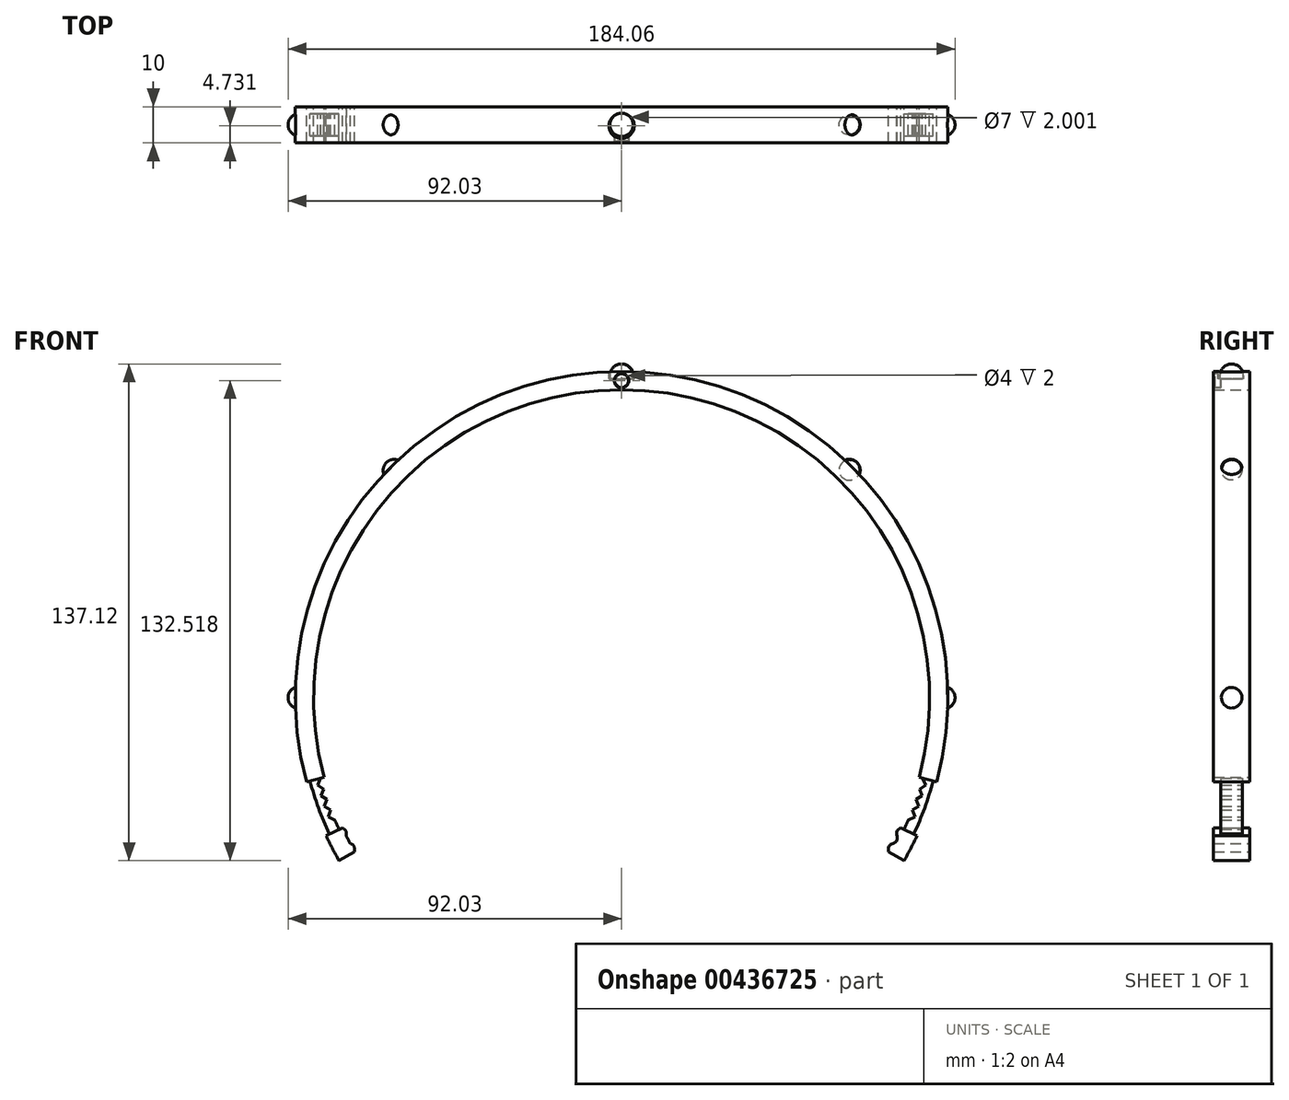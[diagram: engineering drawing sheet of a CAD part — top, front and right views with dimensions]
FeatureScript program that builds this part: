
annotation { "Feature Type Name" : "Feature", "Feature Type Description" : "" }
export const myFeature = defineFeature(function(context is Context, id is Id, definition is map)
    precondition{}
    {
        {
            var Q0;
            Q0=qCreatedBy(makeId("Front.planeOp"),FACE);
            var sketch = newSketch(context, id + "F0", { "sketchPlane" : qUnion([Q0])});
            skArc(sketch, "E0", {"start": v(82.1, -22) * mm, "mid": v(0, 85) * mm, "end": v(-82.1, -22) * mm});
            skArc(sketch, "E1", {"start": v(86.93, -23.3) * mm, "mid": v(0, 90) * mm, "end": v(-86.93, -23.3) * mm});
            skLineSegment(sketch, "E2", {"start": v(-86.93, -23.3) * mm, "end": v(-82.1, -22) * mm});
            skLineSegment(sketch, "E3", {"start": v(82.1, -22) * mm, "end": v(86.93, -23.3) * mm});
            skSolve(sketch);
        }
        {
            var Q0;
            Q0=makeQuery(id+"F0.imprint","IMPRINT",FACE,{"disambiguationData":[TD([[makeQuery(id+"F0.imprint","IMPRINT",EDGE,{"derivedFrom":sQuery(id+"F0.wireOp",EDGE,"E0")}),-1.0]])]});
            extrude(context, id + "F1", {"entities" : qUnion([Q0]), "depth" : 10 * mm});
        }
        {
            var Q0;
            Q0=qCreatedBy(makeId("Front.planeOp"),FACE);
            cPlane(context, id + "F2", {"entities" : qUnion([Q0]), "cplaneType" : CPlaneType.OFFSET, "offset" : 2 * mm, "width" : 150 * mm, "height" : 150 * mm});
        }
        {
            var Q0;
            Q0=qCreatedBy(id+"F2.planeOp",FACE);
            var sketch = newSketch(context, id + "F3", { "sketchPlane" : qUnion([Q0])});
            skLineSegment(sketch, "E4", {"start": v(83.07, -22.26) * mm, "end": v(85.97, -23.03) * mm});
            skArc(sketch, "E5", {"start": v(77.94, -36.35) * mm, "mid": v(78.53, -35.07) * mm, "end": v(79.09, -33.78) * mm});
            skLineSegment(sketch, "E6", {"start": v(83.07, -22.26) * mm, "end": v(83.88, -24.09) * mm});
            skLineSegment(sketch, "E7", {"start": v(83.88, -24.09) * mm, "end": v(82.22, -25.2) * mm});
            skLineSegment(sketch, "E8", {"start": v(82.22, -25.2) * mm, "end": v(82.97, -27.06) * mm});
            skLineSegment(sketch, "E9", {"start": v(82.97, -27.06) * mm, "end": v(81.27, -28.12) * mm});
            skLineSegment(sketch, "E10", {"start": v(81.27, -28.12) * mm, "end": v(82.04, -29.97) * mm});
            skLineSegment(sketch, "E11", {"start": v(82.04, -29.97) * mm, "end": v(80.25, -30.92) * mm});
            skLineSegment(sketch, "E12", {"start": v(80.25, -30.92) * mm, "end": v(80.94, -32.92) * mm});
            skLineSegment(sketch, "E13", {"start": v(80.94, -32.92) * mm, "end": v(79.09, -33.78) * mm});
            skLineSegment(sketch, "E14.MirrorCS", {"start": v(-83.88, -24.09) * mm, "end": v(-82.22, -25.2) * mm});
            skLineSegment(sketch, "E15.MirrorCS", {"start": v(-82.22, -25.2) * mm, "end": v(-82.97, -27.06) * mm});
            skLineSegment(sketch, "E16.MirrorCS", {"start": v(-80.25, -30.92) * mm, "end": v(-80.94, -32.92) * mm});
            skLineSegment(sketch, "E17.MirrorCS", {"start": v(-83.07, -22.26) * mm, "end": v(-85.97, -23.03) * mm});
            skLineSegment(sketch, "E18.MirrorCS", {"start": v(-83.07, -22.26) * mm, "end": v(-83.88, -24.09) * mm});
            skLineSegment(sketch, "E19.MirrorCS", {"start": v(-80.94, -32.92) * mm, "end": v(-79.09, -33.78) * mm});
            skLineSegment(sketch, "E20.MirrorCS", {"start": v(-82.97, -27.06) * mm, "end": v(-81.27, -28.12) * mm});
            skLineSegment(sketch, "E21.MirrorCS", {"start": v(-81.27, -28.12) * mm, "end": v(-82.04, -29.97) * mm});
            skLineSegment(sketch, "E22.MirrorCS", {"start": v(-82.04, -29.97) * mm, "end": v(-80.25, -30.92) * mm});
            skArc(sketch, "E23.MirrorCS", {"start": v(-77.94, -36.35) * mm, "mid": v(-78.53, -35.07) * mm, "end": v(-79.09, -33.78) * mm});
            skArc(sketch, "E24.MirrorCS", {"start": v(-80.66, -37.61) * mm, "mid": v(-83.63, -30.44) * mm, "end": v(-85.97, -23.03) * mm});
            skLineSegment(sketch, "E25", {"start": v(77.94, -36.35) * mm, "end": v(80.66, -37.61) * mm});
            skLineSegment(sketch, "E26", {"start": v(-77.94, -36.35) * mm, "end": v(-80.66, -37.61) * mm});
            skArc(sketch, "E27", {"start": v(85.97, -23.03) * mm, "mid": v(83.63, -30.44) * mm, "end": v(80.66, -37.61) * mm});
            skSolve(sketch);
        }
        {
            var Q0;
            Q0 = qSketchRegion(id + "F3", true);
            extrude(context, id + "F4", {"entities" : qUnion([Q0]), "operationType" : NewBodyOperationType.ADD, "depth" : 6 * mm});
        }
        {
            var Q0;
            Q0=qCreatedBy(makeId("Front.planeOp"),FACE);
            var sketch = newSketch(context, id + "F5", { "sketchPlane" : qUnion([Q0])});
            skArc(sketch, "E28", {"start": v(-81.57, -38.04) * mm, "mid": v(-79.83, -41.56) * mm, "end": v(-77.94, -45) * mm});
            skArc(sketch, "E29", {"start": v(-77.04, -35.92) * mm, "mid": v(-75.4, -39.25) * mm, "end": v(-73.61, -42.5) * mm});
            skLineSegment(sketch, "E30", {"start": v(77.04, -35.92) * mm, "end": v(81.57, -38.04) * mm});
            skLineSegment(sketch, "E31", {"start": v(-77.04, -35.92) * mm, "end": v(-81.57, -38.04) * mm});
            skLineSegment(sketch, "E32", {"start": v(-73.61, -42.5) * mm, "end": v(-77.94, -45) * mm});
            skLineSegment(sketch, "E33", {"start": v(73.61, -42.5) * mm, "end": v(77.94, -45) * mm});
            skArc(sketch, "E34.trimOffspring", {"start": v(77.94, -45) * mm, "mid": v(79.83, -41.56) * mm, "end": v(81.57, -38.04) * mm});
            skFitSpline(sketch, "E35", {"points": [v(77.04, -35.92) * mm, v(75.98, -37.05) * mm, v(75.89, -39.57) * mm, v(74.1, -40.64) * mm, v(73.61, -42.5) * mm], "startDerivative": vector(-6.4, -3.83) * mm, "endDerivative": vector(-0.17, -8.9) * mm});
            skFitSpline(sketch, "E36.MirrorCS", {"points": [v(-77.04, -35.92) * mm, v(-75.98, -37.05) * mm, v(-75.89, -39.57) * mm, v(-74.1, -40.64) * mm, v(-73.61, -42.5) * mm], "startDerivative": vector(6.4, -3.83) * mm, "endDerivative": vector(0.17, -8.9) * mm});
            skArc(sketch, "E37.MirrorCS", {"start": v(-77.94, -45) * mm, "mid": v(-79.83, -41.56) * mm, "end": v(-81.57, -38.04) * mm});
            skSolve(sketch);
        }
        {
            var Q0;
            Q0 = qSketchRegion(id + "F5", true);
            extrude(context, id + "F6", {"entities" : qUnion([Q0]), "depth" : 10 * mm});
        }
        {
            var Q0;
            Q0=makeQuery(id+"F1.opExtrude","CAP_FACE",FACE,{"disambiguationData":[OSD([sQuery(id+"F0.wireOp",EDGE,"E0"),sQuery(id+"F0.wireOp",EDGE,"E1"),sQuery(id+"F0.wireOp",EDGE,"E2"),sQuery(id+"F0.wireOp",EDGE,"E3")])],"isStart":false});
            var sketch = newSketch(context, id + "F7", { "sketchPlane" : qUnion([Q0])});
            skCircle(sketch, "E38", {"center": v(0, 87.52) * mm, "radius": 2 * mm});
            skCircle(sketch, "E39", {"center": v(0, 87.52) * mm, "radius": 1.9 * mm});
            skSolve(sketch);
        }
        {
            var Q0;
            Q0 = qSketchRegion(id + "F7", true);
            extrude(context, id + "F8", {"entities" : qUnion([Q0]), "operationType" : NewBodyOperationType.REMOVE, "oppositeDirection" : true, "depth" : 2 * mm});
        }
        {
            var Q0;
            Q0=qCreatedBy(makeId("Top.planeOp"),FACE);
            cPlane(context, id + "F9", {"entities" : qUnion([Q0]), "cplaneType" : CPlaneType.OFFSET, "offset" : 90 * mm, "width" : 150 * mm, "height" : 150 * mm});
        }
        {
            var Q0;
            Q0=qCreatedBy(id+"F9.planeOp",FACE);
            var sketch = newSketch(context, id + "F10", { "sketchPlane" : qUnion([Q0])});
            skCircle(sketch, "E40", {"center": v(0, -5.27) * mm, "radius": 3.5 * mm});
            skSolve(sketch);
        }
        {
            var Q0;
            Q0 = qSketchRegion(id + "F10", true);
            extrude(context, id + "F11", {"entities" : qUnion([Q0]), "operationType" : NewBodyOperationType.REMOVE, "oppositeDirection" : true, "depth" : 2 * mm});
        }
        {
            var Q0;
            Q0=qCreatedBy(makeId("Front.planeOp"),FACE);
            cPlane(context, id + "F12", {"entities" : qUnion([Q0]), "cplaneType" : CPlaneType.OFFSET, "offset" : 5 * mm, "width" : 150 * mm, "height" : 150 * mm});
        }
        {
            var Q0;
            Q0=qCreatedBy(id+"F12.planeOp",FACE);
            var sketch = newSketch(context, id + "F13", { "sketchPlane" : qUnion([Q0])});
            skLineSegment(sketch, "E41.0", {"start": v(0, 88) * mm, "end": v(3.22, 88) * mm});
            skLineSegment(sketch, "E42", {"start": v(3.22, 88) * mm, "end": v(3.22, 88.9) * mm});
            skLineSegment(sketch, "E43", {"start": v(0, 88) * mm, "end": v(0, 92.12) * mm});
            skArc(sketch, "E44", {"start": v(3.22, 88.9) * mm, "mid": v(2.28, 91.18) * mm, "end": v(0, 92.12) * mm});
            skPoint(sketch, "E45.orphan", {"position": v(-3.5, 88) * mm});
            skPoint(sketch, "E46.orphan", {"position": v(3.5, 88) * mm});
            skSolve(sketch);
        }
        {
            var Q0;
            Q0 = qSketchRegion(id + "F13", true);
            var Q1;
            Q1=sQuery(id+"F13.wireOp",EDGE,"E43");
            revolve(context, id + "F14", {"operationType" : NewBodyOperationType.ADD, "entities" : qUnion([Q0]), "axis" : qUnion([Q1]), "revolveType" : RevolveType.FULL});
        }
        {
            var Q0;
            Q0=qCreatedBy(id+"F12.planeOp",FACE);
            var sketch = newSketch(context, id + "F15", { "sketchPlane" : qUnion([Q0])});
            skLineSegment(sketch, "E47", {"start": v(86.5, 0) * mm, "end": v(86.5, 3) * mm});
            skLineSegment(sketch, "E48", {"start": v(86.5, 3) * mm, "end": v(89.03, 3) * mm});
            skLineSegment(sketch, "E49", {"start": v(86.5, 0) * mm, "end": v(92.03, 0) * mm});
            skArc(sketch, "E50", {"start": v(89.03, 3) * mm, "mid": v(91.15, 2.12) * mm, "end": v(92.03, 0) * mm});
            skLineSegment(sketch, "E51.MirrorCS", {"start": v(-86.5, 0) * mm, "end": v(-92.03, 0) * mm});
            skLineSegment(sketch, "E52.MirrorCS", {"start": v(-86.5, 0) * mm, "end": v(-86.5, 3) * mm});
            skLineSegment(sketch, "E53.MirrorCS", {"start": v(-86.5, 3) * mm, "end": v(-89.03, 3) * mm});
            skArc(sketch, "E54.MirrorCS", {"start": v(-89.03, 3) * mm, "mid": v(-91.15, 2.12) * mm, "end": v(-92.03, 0) * mm});
            skSolve(sketch);
        }
        {
            var Q0;
            Q0 = qSketchRegion(id + "F15", true);
            var Q1;
            Q1=sQuery(id+"F15.wireOp",EDGE,"E49");
            revolve(context, id + "F16", {"operationType" : NewBodyOperationType.ADD, "entities" : qUnion([Q0]), "axis" : qUnion([Q1]), "revolveType" : RevolveType.FULL});
        }
        {
            var Q0;
            Q0=qCreatedBy(id+"F12.planeOp",FACE);
            var sketch = newSketch(context, id + "F17", { "sketchPlane" : qUnion([Q0])});
            skLineSegment(sketch, "E55", {"start": v(61.36, 61.36) * mm, "end": v(59.23, 63.48) * mm});
            skLineSegment(sketch, "E56", {"start": v(61.36, 61.36) * mm, "end": v(64.94, 64.94) * mm});
            skLineSegment(sketch, "E57", {"start": v(59.23, 63.48) * mm, "end": v(60.76, 65) * mm});
            skArc(sketch, "E58", {"start": v(60.76, 65) * mm, "mid": v(62.86, 65.86) * mm, "end": v(64.94, 64.94) * mm});
            skSolve(sketch);
        }
        {
            var Q0;
            Q0 = qSketchRegion(id + "F17", true);
            var Q1;
            Q1=sQuery(id+"F17.wireOp",EDGE,"E56");
            revolve(context, id + "F18", {"operationType" : NewBodyOperationType.ADD, "entities" : qUnion([Q0]), "axis" : qUnion([Q1]), "revolveType" : RevolveType.FULL});
        }
        {
            var Q0;
            Q0=qCreatedBy(id+"F12.planeOp",FACE);
            var sketch = newSketch(context, id + "F19", { "sketchPlane" : qUnion([Q0])});
            skLineSegment(sketch, "E59", {"start": v(-61.52, 61.52) * mm, "end": v(-59.4, 63.64) * mm});
            skLineSegment(sketch, "E60", {"start": v(-61.52, 61.52) * mm, "end": v(-64.9, 64.9) * mm});
            skLineSegment(sketch, "E61", {"start": v(-59.4, 63.64) * mm, "end": v(-60.66, 64.9) * mm});
            skArc(sketch, "E62", {"start": v(-60.66, 64.9) * mm, "mid": v(-62.78, 65.78) * mm, "end": v(-64.9, 64.9) * mm});
            skSolve(sketch);
        }
        {
            var Q0;
            Q0 = qSketchRegion(id + "F19", true);
            var Q1;
            Q1=sQuery(id+"F19.wireOp",EDGE,"E60");
            revolve(context, id + "F20", {"operationType" : NewBodyOperationType.ADD, "entities" : qUnion([Q0]), "axis" : qUnion([Q1]), "revolveType" : RevolveType.FULL});
        }
        {
            var Q0;
            Q0=makeQuery(id+"F8.boolean.opBoolean","SPLIT",FACE,{"disambiguationData":[TD([makeQuery(id+"F8.opExtrude","SWEPT_FACE",FACE,{"disambiguationData":[OSD([sQuery(id+"F7.wireOp",EDGE,"E39")])]})])],"derivedFrom":makeQuery(id+"F1.opExtrude","CAP_FACE",FACE,{"disambiguationData":[OSD([sQuery(id+"F0.wireOp",EDGE,"E0"),sQuery(id+"F0.wireOp",EDGE,"E1"),sQuery(id+"F0.wireOp",EDGE,"E2"),sQuery(id+"F0.wireOp",EDGE,"E3")])],"isStart":false})});
            var sketch = newSketch(context, id + "F21", { "sketchPlane" : qUnion([Q0])});
            skCircle(sketch, "E63.0.0", {"center": v(0, 87.52) * mm, "radius": 1.9 * mm});
            skSolve(sketch);
        }
        {
            var Q0;
            Q0=makeQuery(id+"F21.imprint","IMPRINT",FACE,{"disambiguationData":[TD([[makeQuery(id+"F21.imprint","IMPRINT",EDGE,{"derivedFrom":sQuery(id+"F21.wireOp",EDGE,"E63.0.0")}),1.0]])]});
            extrude(context, id + "F22", {"entities" : qUnion([Q0]), "operationType" : NewBodyOperationType.REMOVE, "oppositeDirection" : true, "depth" : 0.5 * mm});
        }
    });
